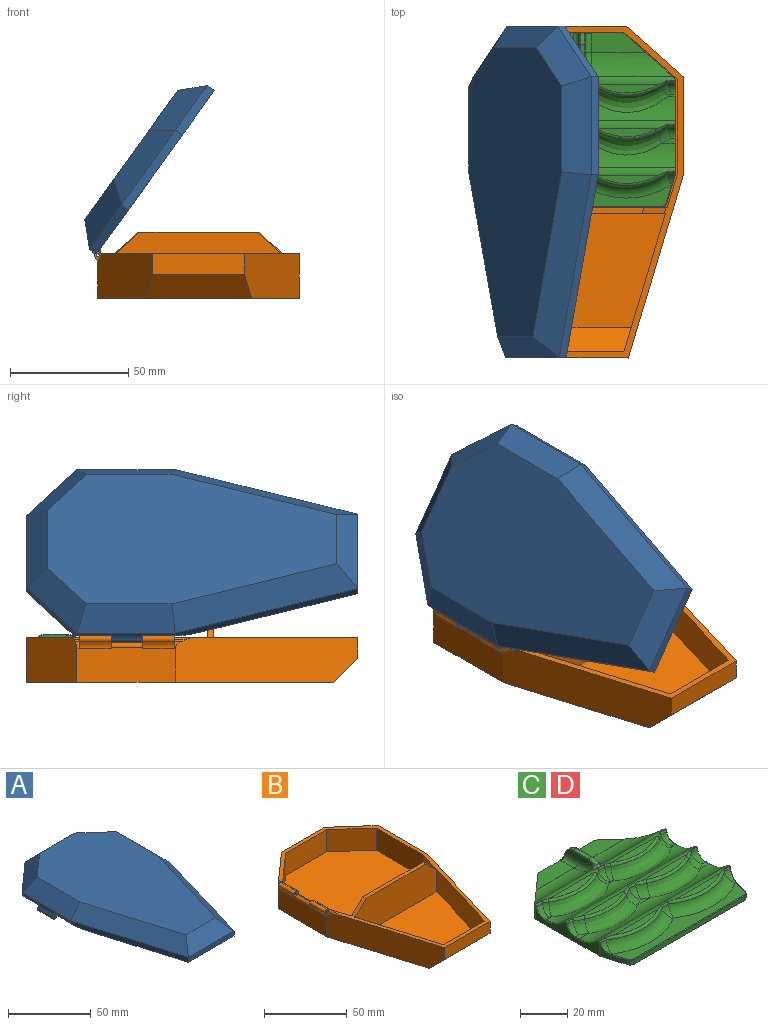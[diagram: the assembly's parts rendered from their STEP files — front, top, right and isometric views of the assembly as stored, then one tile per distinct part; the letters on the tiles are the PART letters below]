
ASSEMBLY  parts=4 mates=3
PART A: 45 faces, bbox 89.1x142.7x17.2 mm
  f0: plane 0.12x0mm, normal (0,1,0), area 0mm2, adj f8,f42
  f1: plane 0.12x0mm, normal (0,-1,0), area 0mm2, adj f8,f42
  f2: cylinder r=1.42mm len=13.33mm, axis (0,-1,0), area 61.4mm2, adj f4,f40,f41,f42
  f3: cylinder r=0.64mm len=13.33mm, axis (0,-1,0), area 53.2mm2, adj f40,f41
  f4: cylinder r=5.08mm len=13.33mm, axis (0,1,0), area 26.1mm2, adj f2,f5,f40,f41
  f5: plane 40x1.11mm, normal (1,0,0), area 43.4mm2, adj f4,f16,f22,f27,f40,f41,f43,f44
  f6: plane 140.08x81.78mm, normal (0,0,-1), area 825.5mm2, adj f7,f9,f10,f11,f12,f13,f14,f16
  f7: plane 24.08x21.4mm, normal (-0.66,0.75,0), area 115.7mm2, adj f6,f8,f14,f35,f44
  f8: plane 41.51x0.35mm, normal (-1,0,0), area 12.9mm2, adj f0,f1,f7,f9,f37,f42,f43,f44
  f9: plane 79.74x25.73mm, normal (-0.96,-0.29,0), area 289.2mm2, adj f6,f8,f10,f39,f43
  f10: plane 38.78x3.65mm, normal (0,-1,0), area 141.5mm2, adj f6,f9,f11,f38
  f11: plane 77.17x23.15mm, normal (0.96,-0.29,0), area 294.1mm2, adj f6,f10,f12,f36
  f12: plane 41.51x3.65mm, normal (1,0,0), area 151.5mm2, adj f6,f11,f13,f34
  f13: plane 24.07x21.4mm, normal (0.66,0.75,0), area 117.6mm2, adj f6,f12,f14,f32
  f14: plane 36.93x3.65mm, normal (0,1,0), area 134.8mm2, adj f6,f7,f13,f33
  f15: plane 122.3x67.3mm, normal (0,0,1), area 6472mm2, adj f32,f33,f34,f35,f36,f37,f38,f39
  f16: plane 22.64x20.14mm, normal (0.66,-0.75,0), area 33.4mm2, adj f5,f6,f17,f25,f44
  f17: plane 35x1.11mm, normal (0,-1,0), area 38.9mm2, adj f6,f16,f18,f24
  f18: plane 22.5x20mm, normal (-0.66,-0.75,0), area 33.4mm2, adj f6,f17,f19,f26
  f19: plane 40x1.11mm, normal (-1,0,0), area 44.4mm2, adj f6,f18,f20,f28
  f20: plane 75x22.5mm, normal (-0.96,0.29,0), area 86.9mm2, adj f6,f19,f21,f30
  f21: plane 35x1.11mm, normal (0,1,0), area 38.9mm2, adj f6,f20,f22,f31
  f22: plane 75.35x22.85mm, normal (0.96,0.29,0), area 86.9mm2, adj f5,f6,f21,f29,f43
  f23: plane 117.22x62.22mm, normal (0,0,-1), area 5673.4mm2, adj f24,f25,f26,f27,f28,f29,f30,f31
  f24: plane 35x8.89mm, normal (0,-0.71,-0.71), area 397.5mm2, adj f17,f23,f25,f26
  f25: plane 25.88x23.99mm, normal (0.47,-0.53,-0.71), area 332.1mm2, adj f16,f23,f24,f27
  f26: plane 25.88x23.99mm, normal (-0.47,-0.53,-0.71), area 332.1mm2, adj f18,f23,f24,f28
  f27: plane 40x8.89mm, normal (0.71,0,-0.71), area 469.6mm2, adj f5,f23,f25,f29
  f28: plane 40x8.89mm, normal (-0.71,0,-0.71), area 469.6mm2, adj f19,f23,f26,f30
  f29: plane 76.3x29.11mm, normal (0.68,0.2,-0.71), area 934.7mm2, adj f22,f23,f27,f31
  f30: plane 76.3x29.11mm, normal (-0.68,0.2,-0.71), area 934.7mm2, adj f20,f23,f28,f31
  f31: plane 35x8.89mm, normal (0,0.71,-0.71), area 356.9mm2, adj f21,f23,f29,f30
  f32: plane 27.45x25.39mm, normal (0.47,0.53,0.71), area 358.6mm2, adj f13,f15,f33,f34
  f33: plane 36.93x8.89mm, normal (0,0.71,0.71), area 421.8mm2, adj f14,f15,f32,f35
  f34: plane 41.51x8.89mm, normal (0.71,0,0.71), area 488.6mm2, adj f12,f15,f32,f36
  f35: plane 27.45x25.39mm, normal (-0.47,0.53,0.71), area 358.6mm2, adj f7,f15,f33,f37
  f36: plane 78.47x29.76mm, normal (0.68,-0.2,0.71), area 963.1mm2, adj f11,f15,f34,f38
  f37: plane 41.51x8.89mm, normal (-0.71,0,0.71), area 488.6mm2, adj f8,f15,f35,f39
  f38: plane 38.78x8.89mm, normal (0,-0.71,0.71), area 404.4mm2, adj f10,f15,f36,f39
  f39: plane 78.47x29.76mm, normal (-0.68,-0.2,0.71), area 963.1mm2, adj f9,f15,f37,f38
  f40: plane 5.49x4.09mm, normal (0,1,0), area 7.4mm2, adj f2,f3,f4,f5,f42,f44
  f41: plane 5.48x4.09mm, normal (0,-1,0), area 7.4mm2, adj f2,f3,f4,f5,f42,f43
  f42: cylinder r=5.08mm len=13.33mm, axis (0,-1,0), area 45.6mm2, adj f0,f1,f2,f8,f40,f41
  f43: bspline ~27.18x3.3mm, area 92mm2, adj f5,f6,f8,f9,f22,f41
  f44: bspline ~19.15x3.3mm, area 72.6mm2, adj f5,f6,f7,f8,f16,f40
PART B: 49 faces, bbox 86.5x140.1x27.9 mm
  f0: plane 58.42x17.53mm, normal (-0.96,0.29,0), area 943.3mm2, adj f22,f25,f31,f45,f47
  f1: plane 16.35x14.04mm, normal (0.96,0.29,0), area 239.7mm2, adj f8,f24,f31,f46
  f2: plane 5.48x3.85mm, normal (0,-1,0), area 6.5mm2, adj f3,f4,f5,f29,f32,f35,f36,f39
  f3: plane 41.51x14.93mm, normal (-1,0,0), area 599.5mm2, adj f2,f9,f10,f11,f26,f27,f28,f29
  f4: cylinder r=1.42mm len=13.33mm, axis (0,-1,0), area 54.6mm2, adj f2,f27,f29,f36
  f5: cylinder r=0.64mm len=13.33mm, axis (0,-1,0), area 53.2mm2, adj f2,f27
  f6: cylinder r=1.42mm len=13.33mm, axis (0,-1,0), area 54.6mm2, adj f9,f26,f28,f37
  f7: cylinder r=0.64mm len=13.33mm, axis (0,-1,0), area 53.2mm2, adj f9,f26
  f8: plane 40x16.35mm, normal (1,0,0), area 626.6mm2, adj f1,f17,f26,f27,f30,f31,f46
  f9: plane 5.48x3.85mm, normal (0,1,0), area 6.5mm2, adj f3,f6,f7,f28,f33,f34,f37,f38
  f10: plane 24.07x21.4mm, normal (-0.66,0.75,0), area 604.4mm2, adj f3,f16,f31,f33,f34,f38,f44
  f11: plane 77.17x23.15mm, normal (-0.96,-0.29,0), area 1457.3mm2, adj f3,f12,f31,f32,f35,f39,f44,f48
  f12: plane 38.78x8.73mm, normal (0,-1,0), area 338.5mm2, adj f11,f13,f31,f48
  f13: plane 77.17x23.15mm, normal (0.96,-0.29,0), area 1468mm2, adj f12,f14,f31,f44,f48
  f14: plane 41.51x18.89mm, normal (1,0,0), area 784.2mm2, adj f13,f15,f31,f44
  f15: plane 24.07x21.4mm, normal (0.66,0.75,0), area 608.5mm2, adj f14,f16,f31,f44
  f16: plane 36.93x18.89mm, normal (0,1,0), area 697.6mm2, adj f10,f15,f31,f44
  f17: plane 22.5x20mm, normal (0.66,-0.75,0), area 492.2mm2, adj f8,f18,f31,f46
  f18: plane 35x16.35mm, normal (0,-1,0), area 572.2mm2, adj f17,f19,f31,f46
  f19: plane 22.5x20mm, normal (-0.66,-0.75,0), area 492.2mm2, adj f18,f20,f31,f46
  f20: plane 40x16.35mm, normal (-1,0,0), area 654mm2, adj f19,f21,f31,f46
  f21: plane 16.35x14.04mm, normal (-0.96,0.29,0), area 239.7mm2, adj f20,f24,f31,f46
  f22: plane 35x6.19mm, normal (0,1,0), area 216.7mm2, adj f0,f23,f31,f47
  f23: plane 58.42x17.53mm, normal (0.96,0.29,0), area 943.3mm2, adj f22,f25,f31,f45,f47
  f24: plane 71.58x25.34mm, normal (0,1,0), area 1720.4mm2, adj f1,f21,f31,f41,f42,f43,f46
  f25: plane 70.05x25.34mm, normal (0,-1,0), area 1681.8mm2, adj f0,f23,f31,f41,f42,f43,f45
  f26: plane 5.48x3.96mm, normal (0,-1,0), area 9.4mm2, adj f3,f6,f7,f8,f28,f30,f31,f34
  f27: plane 5.48x3.96mm, normal (0,1,0), area 9.4mm2, adj f3,f4,f5,f8,f29,f30,f31,f35
  f28: cylinder r=5.08mm len=13.33mm, axis (0,-1,0), area 45.6mm2, adj f3,f6,f9,f26
  f29: cylinder r=5.08mm len=13.33mm, axis (0,-1,0), area 45.6mm2, adj f2,f3,f4,f27
  f30: plane 13.33x0.64mm, normal (0,0,1), area 8.5mm2, adj f8,f26,f27,f40
  f31: plane 140.08x82.62mm, normal (0,0,1), area 840.3mm2, adj f0,f1,f8,f10,f11,f12,f13,f14
  f32: cylinder r=5.08mm len=2.99mm, axis (0,-1,0), area 3.6mm2, adj f2,f3,f11,f39
  f33: cylinder r=5.08mm len=2.71mm, axis (0,1,0), area 3.9mm2, adj f3,f9,f10,f38
  f34: cylinder r=1.27mm len=16.66mm, axis (0,1,0), area 4.7mm2, adj f9,f10,f26,f31,f37,f38
  f35: cylinder r=1.27mm len=21.92mm, axis (0,1,0), area 10.2mm2, adj f2,f11,f27,f31,f36,f39
  f36: cylinder r=2.54mm len=13.33mm, axis (0,-1,0), area 22.6mm2, adj f2,f4,f27,f35
  f37: cylinder r=2.54mm len=13.33mm, axis (0,-1,0), area 22.6mm2, adj f6,f9,f26,f34
  f38: cylinder r=5.08mm len=2.27mm, axis (0,1,0), area 2.3mm2, adj f9,f10,f33,f34
  f39: cylinder r=5.08mm len=4.6mm, axis (0,-1,0), area 4.3mm2, adj f2,f11,f32,f35
  f40: cylinder r=1.91mm len=13.33mm, axis (0,-1,0), area 39.9mm2, adj f3,f26,f27,f30
  f41: plane 51.79x2.54mm, normal (0,0,1), area 129.6mm2, adj f24,f25,f42,f43
  f42: plane 10.15x8.99mm, normal (-0.68,-0.2,0.71), area 33.7mm2, adj f24,f25,f31,f41
  f43: plane 10.15x8.99mm, normal (0.68,-0.2,0.71), area 33.7mm2, adj f24,f25,f31,f41
  f44: plane 129.92x85.08mm, normal (0,0,-1), area 9191.4mm2, adj f3,f10,f11,f13,f14,f15,f16,f48
  f45: plane 70.05x48.26mm, normal (0,0,1), area 2682mm2, adj f0,f23,f25,f47
  f46: plane 80x74.04mm, normal (0,0,1), area 5414.1mm2, adj f1,f8,f17,f18,f19,f20,f21,f24
  f47: plane 41.1x10.16mm, normal (0,0.71,0.71), area 546.7mm2, adj f0,f22,f23,f45
  f48: plane 44.88x10.16mm, normal (0,-0.71,-0.71), area 601mm2, adj f11,f12,f13,f44
PART C: 152 faces, bbox 84.9x79x9.7 mm
  f0: plane 75.15x9.18mm, normal (0,0,1), area 389.9mm2, adj f27,f28,f29,f30,f31,f116,f119,f121
  f1: plane 12.35x5.29mm, normal (-0.96,-0.29,0), area 33.7mm2, adj f13,f82,f89,f125,f127
  f2: cylinder r=15.24mm len=34.12mm, axis (1,0,0), area 316.2mm2, adj f3,f14,f75,f148,f149
  f3: plane 22.81x8.29mm, normal (0,0,1), area 150.1mm2, adj f2,f14,f15,f85,f150,f151
  f4: plane 26.96x3.76mm, normal (0,0,1), area 67.3mm2, adj f53,f75
  f5: plane 26.91x3.64mm, normal (0,0,1), area 65.6mm2, adj f64,f65,f67,f74
  f6: plane 26.91x3.53mm, normal (0,0,1), area 64.1mm2, adj f72,f73
  f7: plane 3.32x0.83mm, normal (0,0,1), area 2.2mm2, adj f25,f42,f44,f94
  f8: plane 3.33x0.83mm, normal (0,0,1), area 1.6mm2, adj f25,f47,f48,f49
  f9: plane 5.69x2.1mm, normal (0,0,1), area 7.9mm2, adj f24,f32,f33,f126
  f10: plane 5.69x2.1mm, normal (0,0,1), area 7.9mm2, adj f24,f39,f40,f101
  f11: plane 3.32x0.83mm, normal (0,0,1), area 2.2mm2, adj f25,f41,f43,f113
  f12: plane 22.81x8.29mm, normal (0,0,1), area 150.1mm2, adj f15,f16,f26,f86,f141,f142
  f13: plane 78.73x73.79mm, normal (0,0,-1), area 5309.7mm2, adj f1,f14,f15,f16,f17,f18,f19,f81
  f14: plane 20.55x18.27mm, normal (-0.66,0.75,0), area 91.1mm2, adj f2,f3,f13,f75,f84,f85
  f15: plane 32.66x4.42mm, normal (0,1,0), area 88.9mm2, adj f3,f12,f13,f80,f85,f86,f141,f151
  f16: plane 20.55x18.27mm, normal (0.66,0.75,0), area 91.1mm2, adj f12,f13,f26,f75,f86,f87
  f17: plane 38.11x7.17mm, normal (1,0,0), area 142.3mm2, adj f13,f87,f88,f93,f94,f95,f97,f99
  f18: plane 12.35x5.29mm, normal (0.96,-0.29,0), area 33.7mm2, adj f13,f83,f88,f114,f116
  f19: plane 38.11x7.17mm, normal (-1,0,0), area 142.3mm2, adj f13,f84,f89,f111,f113,f115,f117,f122
  f20: plane 8.07x2.1mm, normal (0,0,1), area 8.8mm2, adj f24,f35,f36,f37
  f21: plane 26.96x3.76mm, normal (0,0,1), area 67.3mm2, adj f56,f75
  f22: plane 26.91x3.53mm, normal (0,0,1), area 64.1mm2, adj f69,f73
  f23: plane 26.91x3.64mm, normal (0,0,1), area 65.6mm2, adj f60,f61,f62,f74
  f24: cylinder r=15.24mm len=78.22mm, axis (1,0,0), area 659.6mm2, adj f9,f10,f20,f34,f38,f73,f102,f128
  f25: cylinder r=15.24mm len=78.22mm, axis (1,0,0), area 536.7mm2, adj f7,f8,f11,f45,f46,f74,f95,f115
  f26: cylinder r=15.24mm len=34.12mm, axis (1,0,0), area 316.2mm2, adj f12,f16,f75,f143,f144
  f27: cylinder r=5.08mm len=4.98mm, axis (1,0,0), area 14.4mm2, adj f0,f28,f68,f127,f129
  f28: torus R=33.65mm, axis (0,0,1), area 257.4mm2, adj f0,f27,f29,f69
  f29: cylinder r=5.08mm len=4.98mm, axis (1,0,0), area 15.3mm2, adj f0,f28,f30,f70
  f30: torus R=33.65mm, axis (0,0,1), area 257.4mm2, adj f0,f29,f31,f72
  f31: cylinder r=5.08mm len=4.98mm, axis (1,0,0), area 14.4mm2, adj f0,f30,f71,f112,f114
  f32: cylinder r=5.08mm len=4.98mm, axis (1,0,0), area 19.1mm2, adj f9,f33,f59,f124
  f33: torus R=33.65mm, axis (0,0,1), area 32.2mm2, adj f9,f32,f34,f60
  f34: bspline ~32.78x10.46mm, area 216.7mm2, adj f24,f33,f35,f61
  f35: torus R=33.65mm, axis (0,0,1), area 32.2mm2, adj f20,f34,f36,f62
  f36: cylinder r=5.08mm len=4.98mm, axis (1,0,0), area 15.3mm2, adj f20,f35,f37,f63
  f37: torus R=33.65mm, axis (0,0,1), area 32.2mm2, adj f20,f36,f38,f64
  f38: bspline ~32.78x10.46mm, area 216.7mm2, adj f24,f37,f39,f65
  f39: torus R=33.65mm, axis (0,0,1), area 32.2mm2, adj f10,f38,f40,f67
  f40: cylinder r=5.08mm len=4.98mm, axis (1,0,0), area 19.1mm2, adj f10,f39,f66,f100
  f41: cylinder r=5.08mm len=4.98mm, axis (1,0,0), area 20.1mm2, adj f11,f43,f52,f109,f111
  f42: cylinder r=5.08mm len=4.98mm, axis (1,0,0), area 20.1mm2, adj f7,f44,f50,f92,f93
  f43: torus R=33.65mm, axis (0,0,1), area 15.2mm2, adj f11,f41,f45,f54
  f44: torus R=33.65mm, axis (0,0,1), area 15.2mm2, adj f7,f42,f46,f51
  f45: bspline ~37.61x12.73mm, area 261.1mm2, adj f25,f43,f47,f56
  f46: bspline ~37.61x12.73mm, area 261.1mm2, adj f25,f44,f48,f53
  f47: torus R=33.65mm, axis (0,0,1), area 15.2mm2, adj f8,f45,f49,f58
  f48: torus R=33.65mm, axis (0,0,1), area 15.2mm2, adj f8,f46,f49,f55
  f49: cylinder r=5.08mm len=4.98mm, axis (1,0,0), area 15.3mm2, adj f8,f47,f48,f57
  f50: cylinder r=1.27mm len=3.69mm, axis (1,0,0), area 3.4mm2, adj f42,f51,f90,f91
  f51: torus R=27.43mm, axis (0,0,-1), area 3.9mm2, adj f44,f50,f53,f75,f90
  f52: cylinder r=1.27mm len=3.69mm, axis (1,0,0), area 3.4mm2, adj f41,f54,f105,f107
  f53: bspline ~32.79x6.3mm, area 48.7mm2, adj f4,f46,f51,f55,f75
  f54: torus R=27.43mm, axis (0,0,-1), area 3.9mm2, adj f43,f52,f56,f75,f105
  f55: torus R=27.43mm, axis (0,0,-1), area 3.9mm2, adj f48,f53,f57,f75
  f56: bspline ~32.79x6.3mm, area 48.7mm2, adj f21,f45,f54,f58,f75
  f57: cylinder r=1.27mm len=4.14mm, axis (1,0,0), area 4.2mm2, adj f49,f55,f58,f75
  f58: torus R=27.43mm, axis (0,0,-1), area 3.9mm2, adj f47,f56,f57,f75
  f59: cylinder r=1.27mm len=3.69mm, axis (1,0,0), area 3.4mm2, adj f32,f60,f118,f122
  f60: torus R=27.43mm, axis (0,0,-1), area 7.7mm2, adj f23,f33,f59,f61,f74,f118
  f61: bspline ~28.93x5.06mm, area 42.8mm2, adj f23,f34,f60,f62
  f62: torus R=27.43mm, axis (0,0,-1), area 7.8mm2, adj f23,f35,f61,f63,f74
  f63: cylinder r=1.27mm len=4.14mm, axis (1,0,0), area 4.2mm2, adj f36,f62,f64,f74
  f64: torus R=27.43mm, axis (0,0,-1), area 7.8mm2, adj f5,f37,f63,f65,f74
  f65: bspline ~28.93x5.06mm, area 42.8mm2, adj f5,f38,f64,f67
  f66: cylinder r=1.27mm len=3.69mm, axis (1,0,0), area 3.4mm2, adj f40,f67,f96,f99
  f67: torus R=27.43mm, axis (0,0,-1), area 7.7mm2, adj f5,f39,f65,f66,f74,f96
  f68: cylinder r=1.27mm len=3.69mm, axis (1,0,0), area 3.4mm2, adj f27,f69,f131,f132,f134
  f69: torus R=27.43mm, axis (0,0,-1), area 59.8mm2, adj f22,f28,f68,f70,f73,f131
  f70: cylinder r=1.27mm len=4.14mm, axis (1,0,0), area 4.2mm2, adj f29,f69,f72,f73
  f71: cylinder r=1.27mm len=3.69mm, axis (1,0,0), area 3.4mm2, adj f31,f72,f103,f108,f110
  f72: torus R=27.43mm, axis (0,0,-1), area 59.8mm2, adj f6,f30,f70,f71,f73,f103
  f73: cylinder r=5.08mm len=78.22mm, axis (1,0,0), area 262.4mm2, adj f6,f22,f24,f69,f70,f72,f103,f104
  f74: cylinder r=5.08mm len=78.22mm, axis (1,0,0), area 262.4mm2, adj f5,f23,f25,f60,f62,f63,f64,f67
  f75: cylinder r=5.08mm len=78.48mm, axis (1,0,0), area 246.4mm2, adj f2,f4,f14,f16,f21,f26,f51,f53
  f76: plane 16.21x3.56mm, normal (-1,0,0), area 44.7mm2, adj f138,f139,f140,f149,f150
  f77: plane 16.21x3.56mm, normal (1,0,0), area 44.7mm2, adj f135,f136,f137,f142,f143
  f78: plane 8.85x2.03mm, normal (0,0,1), area 18mm2, adj f79,f80,f136,f139
  f79: cylinder r=8.89mm len=4.47mm, axis (1,0,0), area 9.5mm2, adj f78,f135,f138,f146
  f80: cylinder r=5.08mm len=5.08mm, axis (-1,0,0), area 15.8mm2, adj f15,f78,f137,f140,f141,f151
  f81: plane 66.24x2.29mm, normal (0,-1,0), area 151.4mm2, adj f13,f82,f83,f121
  f82: cylinder r=2.54mm len=2.43mm, axis (0,0,1), area 7.4mm2, adj f1,f13,f81,f123
  f83: cylinder r=2.54mm len=2.43mm, axis (0,0,1), area 7.4mm2, adj f13,f18,f81,f119
  f84: cylinder r=2.54mm len=7.32mm, axis (0,0,1), area 15.1mm2, adj f13,f14,f19,f75,f107,f109
  f85: cylinder r=2.54mm len=2.54mm, axis (0,0,1), area 4.7mm2, adj f3,f13,f14,f15
  f86: cylinder r=2.54mm len=2.54mm, axis (0,0,1), area 4.7mm2, adj f12,f13,f15,f16
  f87: cylinder r=2.54mm len=7.32mm, axis (0,0,1), area 15.1mm2, adj f13,f16,f17,f75,f91,f92
  f88: cylinder r=2.54mm len=7.01mm, axis (0,0,1), area 4.6mm2, adj f13,f17,f18,f110,f112
  f89: cylinder r=2.54mm len=7.01mm, axis (0,0,1), area 4.6mm2, adj f1,f13,f19,f129,f132
  f90: cylinder r=0.25mm len=3.81mm, axis (-1,0,0), area 0.8mm2, adj f50,f51,f75,f91
  f91: bspline ~1.25x1.18mm, area 0.4mm2, adj f50,f75,f87,f90,f92
  f92: bspline ~0.33x0.31mm, area 0mm2, adj f42,f87,f91,f93
  f93: torus R=5.33mm, axis (1,0,0), area 2.8mm2, adj f17,f42,f92,f94
  f94: cylinder r=0.25mm len=0.83mm, axis (0,1,0), area 0.3mm2, adj f7,f17,f93,f95
  f95: torus R=15.49mm, axis (1,0,0), area 4.4mm2, adj f17,f25,f94,f97
  f96: cylinder r=0.25mm len=3.69mm, axis (-1,0,0), area 0.8mm2, adj f66,f67,f74,f98
  f97: torus R=4.83mm, axis (1,0,0), area 0.9mm2, adj f17,f74,f95,f98
  f98: sphere r=0.25mm, area 0.1mm2, adj f96,f97,f99
  f99: torus R=1.02mm, axis (1,0,0), area 0.3mm2, adj f17,f66,f98,f100
  f100: torus R=5.33mm, axis (1,0,0), area 2.8mm2, adj f17,f40,f99,f101
  f101: cylinder r=0.25mm len=2.1mm, axis (0,1,0), area 0.8mm2, adj f10,f17,f100,f102
  f102: torus R=15.49mm, axis (1,0,0), area 4.4mm2, adj f17,f24,f101,f104
  f103: cylinder r=0.25mm len=3.69mm, axis (-1,0,0), area 0.8mm2, adj f71,f72,f73,f106
  f104: torus R=4.83mm, axis (1,0,0), area 0.9mm2, adj f17,f73,f102,f106
  f105: cylinder r=0.25mm len=3.81mm, axis (-1,0,0), area 0.8mm2, adj f52,f54,f75,f107
  f106: sphere r=0.25mm, area 0.1mm2, adj f103,f104,f108
  f107: bspline ~1.18x1.18mm, area 0.4mm2, adj f52,f75,f84,f105,f109
  f108: torus R=1.02mm, axis (1,0,0), area 0.1mm2, adj f17,f71,f106,f110
  f109: bspline ~0.32x0.31mm, area 0mm2, adj f41,f84,f107,f111
  f110: bspline ~0.91x0.54mm, area 0.2mm2, adj f71,f88,f108,f112
  f111: torus R=5.33mm, axis (-1,0,0), area 2.8mm2, adj f19,f41,f109,f113
  f112: bspline ~2.54x1.12mm, area 0.5mm2, adj f31,f88,f110,f114
  f113: cylinder r=0.25mm len=0.83mm, axis (0,-1,0), area 0.3mm2, adj f11,f19,f111,f115
  f114: bspline ~5.94x3.59mm, area 2.2mm2, adj f18,f31,f112,f116
  f115: torus R=15.49mm, axis (-1,0,0), area 4.4mm2, adj f19,f25,f113,f117
  f116: cylinder r=0.25mm len=7.62mm, axis (0.29,0.96,0), area 3.1mm2, adj f0,f18,f114,f119
  f117: torus R=4.83mm, axis (-1,0,0), area 0.9mm2, adj f19,f74,f115,f120
  f118: cylinder r=0.25mm len=3.69mm, axis (-1,0,0), area 0.8mm2, adj f59,f60,f74,f120
  f119: torus R=2.29mm, axis (0,0,1), area 1.2mm2, adj f0,f83,f116,f121
  f120: sphere r=0.25mm, area 0.1mm2, adj f117,f118,f122
  f121: cylinder r=0.25mm len=66.24mm, axis (1,0,0), area 26.4mm2, adj f0,f81,f119,f123
  f122: torus R=1.02mm, axis (-1,0,0), area 0.3mm2, adj f19,f59,f120,f124
  f123: torus R=2.29mm, axis (0,0,1), area 1.2mm2, adj f0,f82,f121,f125
  f124: torus R=5.33mm, axis (-1,0,0), area 2.8mm2, adj f19,f32,f122,f126
  f125: cylinder r=0.25mm len=7.62mm, axis (0.29,-0.96,0), area 3.1mm2, adj f0,f1,f123,f127
  f126: cylinder r=0.25mm len=2.1mm, axis (0,-1,0), area 0.8mm2, adj f9,f19,f124,f128
  f127: bspline ~5.94x3.59mm, area 2.2mm2, adj f1,f27,f125,f129
  f128: torus R=15.49mm, axis (-1,0,0), area 4.4mm2, adj f19,f24,f126,f130
  f129: bspline ~2.54x1.12mm, area 0.5mm2, adj f27,f89,f127,f132
  f130: torus R=4.83mm, axis (-1,0,0), area 0.9mm2, adj f19,f73,f128,f133
  f131: cylinder r=0.25mm len=3.69mm, axis (-1,0,0), area 0.8mm2, adj f68,f69,f73,f133
  f132: bspline ~0.88x0.67mm, area 0.2mm2, adj f68,f89,f129,f134
  f133: sphere r=0.25mm, area 0.1mm2, adj f130,f131,f134
  f134: torus R=1.02mm, axis (-1,0,0), area 0.1mm2, adj f19,f68,f132,f133
  f135: torus R=8.64mm, axis (-1,0,0), area 1.6mm2, adj f77,f79,f136,f144,f145
  f136: cylinder r=0.25mm len=8.85mm, axis (0,-1,0), area 3.5mm2, adj f77,f78,f135,f137
  f137: torus R=4.83mm, axis (-1,0,0), area 2.7mm2, adj f77,f80,f136,f141
  f138: torus R=8.64mm, axis (-1,0,0), area 1.6mm2, adj f76,f79,f139,f147,f148
  f139: cylinder r=0.25mm len=8.85mm, axis (0,1,0), area 3.5mm2, adj f76,f78,f138,f140
  f140: torus R=4.83mm, axis (-1,0,0), area 2.7mm2, adj f76,f80,f139,f151
  f141: bspline ~5.31x3.18mm, area 1.7mm2, adj f12,f15,f80,f137,f142
  f142: cylinder r=2.54mm len=7.87mm, axis (0,1,0), area 31.4mm2, adj f12,f77,f141,f143
  f143: torus R=12.7mm, axis (-1,0,0), area 40.9mm2, adj f26,f77,f142,f144
  f144: bspline ~2.55x1.95mm, area 0.2mm2, adj f26,f135,f143,f145
  f145: bspline ~4.04x2.93mm, area 6.3mm2, adj f75,f135,f144,f146
  f146: cylinder r=2.54mm len=2.03mm, axis (1,0,0), area 4.1mm2, adj f75,f79,f145,f147
  f147: bspline ~3.82x3.3mm, area 6.3mm2, adj f75,f138,f146,f148
  f148: bspline ~2.6x2.05mm, area 0.2mm2, adj f2,f138,f147,f149
  f149: torus R=12.7mm, axis (-1,0,0), area 40.9mm2, adj f2,f76,f148,f150
  f150: cylinder r=2.54mm len=7.87mm, axis (0,-1,0), area 31.4mm2, adj f3,f76,f149,f151
  f151: bspline ~5.26x3.14mm, area 1.7mm2, adj f3,f15,f80,f140,f150
PART D: same geometry as C
PLACE A rot(axis=(0,-1,0),54.3deg) t=(33.9,26.95,-22.58)mm
PLACE B rot(axis=(0.71,0.21,-0.67),0deg) t=(62.29,26.95,-77.98)mm fixed
PLACE C rot(axis=(0.71,0.21,-0.67),0deg) t=(-26.35,27.38,-71.68)mm
PLACE D t=(-26.35,27.38,-80.52)mm
MATE slider C.f13 <-> B.f46  axis (0,0,-1) through (62.29,122.76,-71.68)mm
MATE revolute A.f2 <-> B.f4  axis (0,-1,0) through (19.75,115.28,-64.81)mm
MATE slider D.f13 <-> B.f46  axis (0,0,-1) through (62.29,122.76,-80.52)mm
